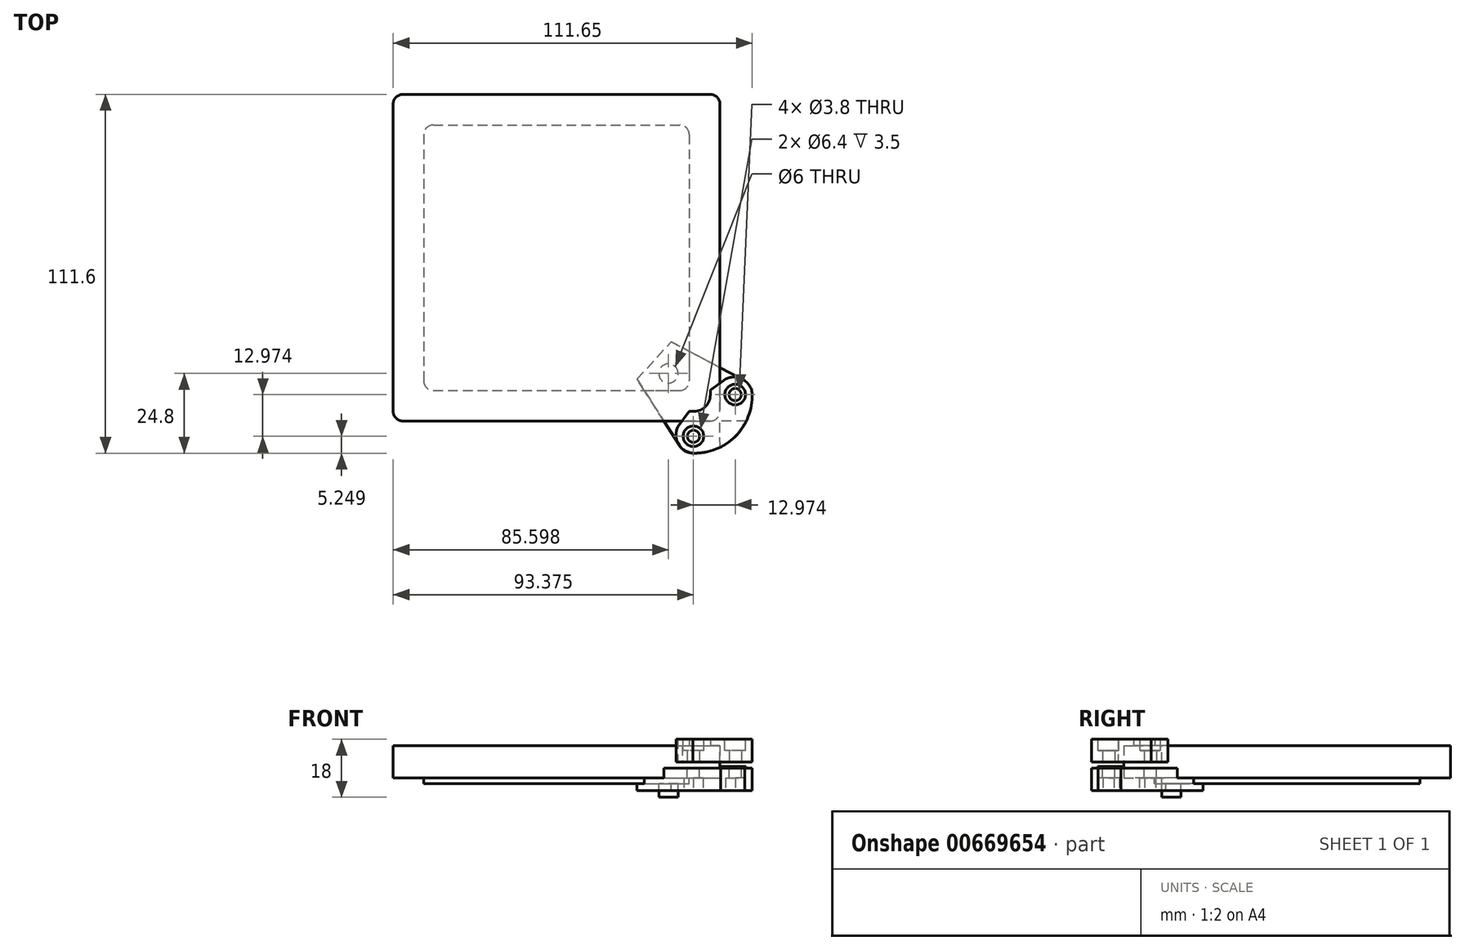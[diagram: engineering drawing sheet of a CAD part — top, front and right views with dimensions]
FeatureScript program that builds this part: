
annotation { "Feature Type Name" : "Feature", "Feature Type Description" : "" }
export const myFeature = defineFeature(function(context is Context, id is Id, definition is map)
    precondition{}
    {
        {
            var Q0;
            Q0=qCreatedBy(makeId("Top.planeOp"),FACE);
            var sketch = newSketch(context, id + "F0", { "sketchPlane" : qUnion([Q0])});
            skLineSegment(sketch, "E0.bottom", {"start": v(-49.2, 52.24) * mm, "end": v(46.4, 52.24) * mm});
            skLineSegment(sketch, "E0.top", {"start": v(-49.2, -49.36) * mm, "end": v(46.4, -49.36) * mm});
            skLineSegment(sketch, "E0.left", {"start": v(-52.2, 49.24) * mm, "end": v(-52.2, -46.36) * mm});
            skLineSegment(sketch, "E0.right", {"start": v(49.4, 49.24) * mm, "end": v(49.4, -46.36) * mm});
            skPoint(sketch, "E1.visualSharp", {"position": v(-52.2, 52.24) * mm});
            skArc(sketch, "E1.filletArc", {"start": v(-49.2, 52.24) * mm, "mid": v(-51.31, 51.36) * mm, "end": v(-52.2, 49.24) * mm});
            skPoint(sketch, "E2.visualSharp", {"position": v(-52.2, -49.36) * mm});
            skArc(sketch, "E2.filletArc", {"start": v(-52.2, -46.36) * mm, "mid": v(-51.31, -48.48) * mm, "end": v(-49.2, -49.36) * mm});
            skPoint(sketch, "E3.visualSharp", {"position": v(49.4, -49.36) * mm});
            skArc(sketch, "E3.filletArc", {"start": v(46.4, -49.36) * mm, "mid": v(48.53, -48.48) * mm, "end": v(49.4, -46.36) * mm});
            skPoint(sketch, "E4.visualSharp", {"position": v(49.4, 52.24) * mm});
            skArc(sketch, "E4.filletArc", {"start": v(49.4, 49.24) * mm, "mid": v(48.53, 51.36) * mm, "end": v(46.4, 52.24) * mm});
            skLineSegment(sketch, "E5.0", {"start": v(-39.7, 42.74) * mm, "end": v(36.9, 42.74) * mm});
            skLineSegment(sketch, "E5.1", {"start": v(-42.7, 39.74) * mm, "end": v(-42.7, -36.86) * mm});
            skLineSegment(sketch, "E5.2", {"start": v(-39.7, -39.86) * mm, "end": v(36.9, -39.86) * mm});
            skLineSegment(sketch, "E5.3", {"start": v(39.9, 39.74) * mm, "end": v(39.9, -36.86) * mm});
            skPoint(sketch, "E6.visualSharp", {"position": v(-42.7, 42.74) * mm});
            skArc(sketch, "E6.filletArc", {"start": v(-39.7, 42.74) * mm, "mid": v(-41.81, 41.86) * mm, "end": v(-42.7, 39.74) * mm});
            skPoint(sketch, "E7.visualSharp", {"position": v(-42.7, -39.86) * mm});
            skArc(sketch, "E7.filletArc", {"start": v(-42.7, -36.86) * mm, "mid": v(-41.81, -38.98) * mm, "end": v(-39.7, -39.86) * mm});
            skPoint(sketch, "E8.visualSharp", {"position": v(39.9, -39.86) * mm});
            skArc(sketch, "E8.filletArc", {"start": v(36.9, -39.86) * mm, "mid": v(39.03, -38.98) * mm, "end": v(39.9, -36.86) * mm});
            skPoint(sketch, "E9.visualSharp", {"position": v(39.9, 42.74) * mm});
            skArc(sketch, "E9.filletArc", {"start": v(39.9, 39.74) * mm, "mid": v(39.03, 41.86) * mm, "end": v(36.9, 42.74) * mm});
            skCircle(sketch, "E10", {"center": v(33.4, -34.56) * mm, "radius": 3 * mm});
            skSolve(sketch);
        }
        {
            var Q0;
            Q0 = qSketchRegion(id + "F0", true);
            var Q1;
            Q1=makeQuery(id+"F0.imprint","IMPRINT",FACE,{"disambiguationData":[TD([[makeQuery(id+"F0.imprint","IMPRINT",EDGE,{"derivedFrom":sQuery(id+"F0.wireOp",EDGE,"E5.0")}),-1.0]])]});
            var Q2;
            Q2=makeQuery(id+"F0.imprint","IMPRINT",FACE,{"disambiguationData":[TD([[makeQuery(id+"F0.imprint","IMPRINT",EDGE,{"derivedFrom":sQuery(id+"F0.wireOp",EDGE,"E10")}),1.0]])]});
            extrude(context, id + "F1", {"entities" : qUnion([Q0, Q1, Q2]), "flatOperationType" : FlatOperationType.REMOVE, "depth" : 10 * mm, "offsetDistance" : 25.4 * mm, "domain" : OperationDomain.MODEL});
        }
        {
            var Q0;
            Q0=makeQuery(id+"F0.imprint","IMPRINT",FACE,{"disambiguationData":[TD([[makeQuery(id+"F0.imprint","IMPRINT",EDGE,{"derivedFrom":sQuery(id+"F0.wireOp",EDGE,"E5.0")}),-1.0]])]});
            extrude(context, id + "F2", {"entities" : qUnion([Q0]), "operationType" : NewBodyOperationType.ADD, "oppositeDirection" : true, "depth" : 1.8 * mm, "offsetDistance" : 25 * mm});
        }
        {
            var Q0;
            Q0=makeQuery(id+"F2.boolean.opBoolean","SPLIT",FACE,{"disambiguationData":[TD([makeQuery(id+"F2.opExtrude","SWEPT_FACE",FACE,{"disambiguationData":[OSD([sQuery(id+"F0.wireOp",EDGE,"E10")])]})])],"derivedFrom":makeQuery(id+"F1.opExtrude","CAP_FACE",FACE,{"disambiguationData":[OSD([sQuery(id+"F0.wireOp",EDGE,"E0.bottom"),sQuery(id+"F0.wireOp",EDGE,"E0.top"),sQuery(id+"F0.wireOp",EDGE,"E0.left"),sQuery(id+"F0.wireOp",EDGE,"E0.right"),sQuery(id+"F0.wireOp",EDGE,"E1.filletArc"),sQuery(id+"F0.wireOp",EDGE,"E2.filletArc"),sQuery(id+"F0.wireOp",EDGE,"E3.filletArc"),sQuery(id+"F0.wireOp",EDGE,"E4.filletArc")])],"isStart":true})});
            var Q1;
            Q1=sQuery(id+"F0.wireOp",EDGE,"E10");
            extrude(context, id + "F3", {"entities" : qUnion([Q0]), "operationType" : NewBodyOperationType.ADD, "surfaceEntities" : qUnion([Q1]), "depth" : 6 * mm, "offsetDistance" : 25 * mm});
        }
        {
            var Q0;
            Q0=qCreatedBy(makeId("Top.planeOp"),FACE);
            var sketch = newSketch(context, id + "F4", { "sketchPlane" : qUnion([Q0])});
            skLineSegment(sketch, "E11.bottom", {"start": v(56.62, -36.5) * mm, "end": v(34.3, -24.68) * mm});
            skLineSegment(sketch, "E11.top", {"start": v(41.5, -59.36) * mm, "end": v(41.18, -59.36) * mm});
            skLineSegment(sketch, "E11.left", {"start": v(59.4, -41.14) * mm, "end": v(59.4, -41.45) * mm});
            skLineSegment(sketch, "E11.right", {"start": v(23.66, -36.34) * mm, "end": v(36.76, -56.93) * mm});
            skArc(sketch, "E12.filletArc", {"start": v(36.76, -56.93) * mm, "mid": v(38.66, -58.71) * mm, "end": v(41.18, -59.36) * mm});
            skArc(sketch, "E13.filletArc", {"start": v(41.5, -59.36) * mm, "mid": v(54.16, -54.11) * mm, "end": v(59.4, -41.45) * mm});
            skArc(sketch, "E14.filletArc", {"start": v(59.4, -41.14) * mm, "mid": v(58.66, -38.43) * mm, "end": v(56.62, -36.5) * mm});
            skCircle(sketch, "E15", {"center": v(54.16, -41.14) * mm, "radius": 1.9 * mm});
            skCircle(sketch, "E16", {"center": v(41.18, -54.11) * mm, "radius": 1.9 * mm});
            skPoint(sketch, "E17", {"position": v(34.3, -24.68) * mm});
            skPoint(sketch, "E18", {"position": v(23.66, -36.34) * mm});
            skLineSegment(sketch, "E19", {"start": v(34.3, -24.68) * mm, "end": v(23.66, -36.34) * mm});
            skPoint(sketch, "E20", {"position": v(41.18, -59.36) * mm});
            skLineSegment(sketch, "E21", {"start": v(30.2, -46.63) * mm, "end": v(45.46, -30.59) * mm, "construction": true});
            skLineSegment(sketch, "E22", {"start": v(37.83, -38.61) * mm, "end": v(28.98, -30.5) * mm, "construction": true});
            skPoint(sketch, "E23", {"position": v(33.4, -34.56) * mm});
            skLineSegment(sketch, "E24", {"start": v(36.76, -56.93) * mm, "end": v(56.62, -36.5) * mm, "construction": true});
            skLineSegment(sketch, "E25", {"start": v(32.03, -49.5) * mm, "end": v(70.12, -49.5) * mm, "construction": true});
            skLineSegment(sketch, "E26", {"start": v(49.4, -63.01) * mm, "end": v(49.4, -15.8) * mm, "construction": true});
            skLineSegment(sketch, "E27", {"start": v(49.4, -49.5) * mm, "end": v(49.4, -57.52) * mm});
            skLineSegment(sketch, "E28", {"start": v(49.4, -49.5) * mm, "end": v(57.5, -49.5) * mm});
            skEllipticalArc(sketch, "E29", {});
            skLineSegment(sketch, "E30", {"start": v(49.4, -57.5) * mm, "end": v(49.4, -49.5) * mm});
            const initialGuessF4  = {"E29": [0.049408, -0.0494937938059676, 0.7031298044576713, -0.7110615149783577, 0.006693227332354382, 0.010739871215108025, 5.730894756647801, 0.562360824754581]};
            skSetInitialGuess(sketch, initialGuessF4);
            skSolve(sketch);
        }
        {
            var Q0;
            Q0 = qSketchRegion(id + "F4", true);
            extrude(context, id + "F5", {"entities" : qUnion([Q0]), "oppositeDirection" : true, "depth" : 7 * mm, "offsetDistance" : 25 * mm});
        }
        {
            var Q0;
            Q0=makeQuery(id+"F5.opExtrude","SWEPT_BODY",BODY,{"disambiguationData":[OSD([sQuery(id+"F4.wireOp",EDGE,"E11.bottom"),sQuery(id+"F4.wireOp",EDGE,"E11.top"),sQuery(id+"F4.wireOp",EDGE,"E11.left"),sQuery(id+"F4.wireOp",EDGE,"E11.right"),sQuery(id+"F4.wireOp",EDGE,"E12.filletArc"),sQuery(id+"F4.wireOp",EDGE,"E13.filletArc"),sQuery(id+"F4.wireOp",EDGE,"E14.filletArc"),sQuery(id+"F4.wireOp",EDGE,"E15"),sQuery(id+"F4.wireOp",EDGE,"E16"),sQuery(id+"F4.wireOp",EDGE,"66c13378-0b8c-4c4a-871f-ac784376b0e9"),sQuery(id+"F4.wireOp",EDGE,"E19")])]});
            transform(context, id + "F6", {"entities" : qUnion([Q0]), "transformType" : TransformType.TRANSLATION_3D, "dx" : 0 * mm, "dy" : 0 * mm, "dz" : 3 * mm, "makeCopy" : false});
        }
        {
            var Q0;
            Q0=makeQuery(id+"F5.opExtrude","CAP_FACE",FACE,{"disambiguationData":[OSD([sQuery(id+"F4.wireOp",EDGE,"E11.bottom"),sQuery(id+"F4.wireOp",EDGE,"E11.top"),sQuery(id+"F4.wireOp",EDGE,"E11.left"),sQuery(id+"F4.wireOp",EDGE,"E11.right"),sQuery(id+"F4.wireOp",EDGE,"E12.filletArc"),sQuery(id+"F4.wireOp",EDGE,"E13.filletArc"),sQuery(id+"F4.wireOp",EDGE,"E14.filletArc"),sQuery(id+"F4.wireOp",EDGE,"E15"),sQuery(id+"F4.wireOp",EDGE,"E16"),sQuery(id+"F4.wireOp",EDGE,"E19")])],"isStart":false});
            var sketch = newSketch(context, id + "F7", { "sketchPlane" : qUnion([Q0])});
            skCircle(sketch, "E31.cCircle", {"center": v(54.16, 41.14) * mm, "radius": 3.4 * mm, "construction": true});
            skLineSegment(sketch, "E31.0", {"start": v(51.2, 42.84) * mm, "end": v(54.16, 44.54) * mm});
            skLineSegment(sketch, "E31.1", {"start": v(54.16, 44.54) * mm, "end": v(57.1, 42.84) * mm});
            skLineSegment(sketch, "E31.2", {"start": v(57.1, 42.84) * mm, "end": v(57.1, 39.43) * mm});
            skLineSegment(sketch, "E31.3", {"start": v(57.1, 39.43) * mm, "end": v(54.16, 37.73) * mm});
            skLineSegment(sketch, "E31.4", {"start": v(54.16, 37.73) * mm, "end": v(51.2, 39.43) * mm});
            skLineSegment(sketch, "E31.5", {"start": v(51.2, 39.43) * mm, "end": v(51.2, 42.84) * mm});
            skCircle(sketch, "E32.cCircle", {"center": v(41.18, 54.11) * mm, "radius": 3.4 * mm, "construction": true});
            skLineSegment(sketch, "E32.0", {"start": v(38.23, 55.81) * mm, "end": v(41.18, 57.52) * mm});
            skLineSegment(sketch, "E32.1", {"start": v(41.18, 57.52) * mm, "end": v(44.13, 55.81) * mm});
            skLineSegment(sketch, "E32.2", {"start": v(44.13, 55.81) * mm, "end": v(44.13, 52.4) * mm});
            skLineSegment(sketch, "E32.3", {"start": v(44.13, 52.4) * mm, "end": v(41.18, 50.7) * mm});
            skLineSegment(sketch, "E32.4", {"start": v(41.18, 50.7) * mm, "end": v(38.23, 52.4) * mm});
            skLineSegment(sketch, "E32.5", {"start": v(38.23, 52.4) * mm, "end": v(38.23, 55.81) * mm});
            skSolve(sketch);
        }
        {
            var Q0;
            Q0 = qSketchRegion(id + "F7", true);
            extrude(context, id + "F8", {"entities" : qUnion([Q0]), "operationType" : NewBodyOperationType.REMOVE, "oppositeDirection" : true, "depth" : 4 * mm, "offsetDistance" : 25 * mm});
        }
        {
            var Q0;
            Q0=makeQuery(id+"F1.opExtrude","CAP_FACE",FACE,{"disambiguationData":[OSD([sQuery(id+"F0.wireOp",EDGE,"E0.bottom"),sQuery(id+"F0.wireOp",EDGE,"E0.top"),sQuery(id+"F0.wireOp",EDGE,"E0.left"),sQuery(id+"F0.wireOp",EDGE,"E0.right"),sQuery(id+"F0.wireOp",EDGE,"E1.filletArc"),sQuery(id+"F0.wireOp",EDGE,"E2.filletArc"),sQuery(id+"F0.wireOp",EDGE,"E3.filletArc"),sQuery(id+"F0.wireOp",EDGE,"E4.filletArc")])],"isStart":false});
            var sketch = newSketch(context, id + "F9", { "sketchPlane" : qUnion([Q0])});
            skArc(sketch, "E33.filletArc", {"start": v(41.06, -59.34) * mm, "mid": v(54.24, -54.07) * mm, "end": v(59.45, -40.86) * mm});
            skPoint(sketch, "E34", {"position": v(34.12, -59.33) * mm});
            skCircle(sketch, "E35", {"center": v(54.16, -41.14) * mm, "radius": 1.9 * mm});
            skCircle(sketch, "E36", {"center": v(41.18, -54.11) * mm, "radius": 1.9 * mm});
            skLineSegment(sketch, "E37", {"start": v(50.52, -36.75) * mm, "end": v(46.4, -39.68) * mm});
            skLineSegment(sketch, "E38", {"start": v(46.4, -39.68) * mm, "end": v(46.4, -41.3) * mm});
            skPoint(sketch, "E39.visualSharp", {"position": v(56.89, -32.2) * mm});
            skArc(sketch, "E39.filletArc", {"start": v(59.45, -40.86) * mm, "mid": v(56.17, -36.21) * mm, "end": v(50.52, -36.75) * mm});
            skLineSegment(sketch, "E40", {"start": v(54.24, -54.07) * mm, "end": v(41.55, -41.44) * mm, "construction": true});
            skLineSegment(sketch, "E41.MirrorCS", {"start": v(39.82, -46.31) * mm, "end": v(41.43, -46.3) * mm});
            skLineSegment(sketch, "E42.MirrorCS", {"start": v(36.37, -51.19) * mm, "end": v(39.82, -46.31) * mm});
            skArc(sketch, "E43.MirrorCS", {"start": v(41.06, -59.34) * mm, "mid": v(36.53, -56.52) * mm, "end": v(36.37, -51.19) * mm});
            skPoint(sketch, "E44.visualSharp", {"position": v(46.4, -46.28) * mm});
            skArc(sketch, "E44.filletArc", {"start": v(41.43, -46.3) * mm, "mid": v(44.95, -44.83) * mm, "end": v(46.4, -41.3) * mm});
            skSolve(sketch);
        }
        {
            var Q0;
            Q0 = qSketchRegion(id + "F9", true);
            extrude(context, id + "F10", {"entities" : qUnion([Q0]), "depth" : 7 * mm, "offsetDistance" : 25 * mm});
        }
        {
            var Q0;
            Q0=makeQuery(id+"F10.opExtrude","CAP_FACE",FACE,{"disambiguationData":[OSD([sQuery(id+"F9.wireOp",EDGE,"a39b41d0-e7ae-40f5-bbe2-d8dd226e776d.bottom"),sQuery(id+"F9.wireOp",EDGE,"a39b41d0-e7ae-40f5-bbe2-d8dd226e776d.top"),sQuery(id+"F9.wireOp",EDGE,"a39b41d0-e7ae-40f5-bbe2-d8dd226e776d.left"),sQuery(id+"F9.wireOp",EDGE,"a39b41d0-e7ae-40f5-bbe2-d8dd226e776d.right"),sQuery(id+"F9.wireOp",EDGE,"845669e1-6970-4c6b-b3a8-32a38f3c468b.filletArc"),sQuery(id+"F9.wireOp",EDGE,"E33.filletArc"),sQuery(id+"F9.wireOp",EDGE,"ea5769c7-4f24-4bfb-a007-04b614ccd4af.filletArc"),sQuery(id+"F9.wireOp",EDGE,"E35"),sQuery(id+"F9.wireOp",EDGE,"E36")])],"isStart":false});
            var sketch = newSketch(context, id + "F11", { "sketchPlane" : qUnion([Q0])});
            skCircle(sketch, "E45", {"center": v(41.18, -54.11) * mm, "radius": 3.2 * mm});
            skCircle(sketch, "E46", {"center": v(54.16, -41.14) * mm, "radius": 3.2 * mm});
            skSolve(sketch);
        }
        {
            var Q0;
            Q0 = qSketchRegion(id + "F11", true);
            extrude(context, id + "F12", {"entities" : qUnion([Q0]), "operationType" : NewBodyOperationType.REMOVE, "oppositeDirection" : true, "depth" : 3.5 * mm, "offsetDistance" : 25 * mm});
        }
        {
            var Q0;
            Q0=makeQuery(id+"F10.opExtrude","SWEPT_BODY",BODY,{"disambiguationData":[OSD([sQuery(id+"F9.wireOp",EDGE,"a39b41d0-e7ae-40f5-bbe2-d8dd226e776d.bottom"),sQuery(id+"F9.wireOp",EDGE,"a39b41d0-e7ae-40f5-bbe2-d8dd226e776d.top"),sQuery(id+"F9.wireOp",EDGE,"a39b41d0-e7ae-40f5-bbe2-d8dd226e776d.left"),sQuery(id+"F9.wireOp",EDGE,"a39b41d0-e7ae-40f5-bbe2-d8dd226e776d.right"),sQuery(id+"F9.wireOp",EDGE,"845669e1-6970-4c6b-b3a8-32a38f3c468b.filletArc"),sQuery(id+"F9.wireOp",EDGE,"E33.filletArc"),sQuery(id+"F9.wireOp",EDGE,"ea5769c7-4f24-4bfb-a007-04b614ccd4af.filletArc"),sQuery(id+"F9.wireOp",EDGE,"E35"),sQuery(id+"F9.wireOp",EDGE,"E36")])]});
            transform(context, id + "F13", {"entities" : qUnion([Q0]), "transformType" : TransformType.TRANSLATION_3D, "dx" : 0 * mm, "dy" : 0 * mm, "dz" : -5 * mm, "makeCopy" : false});
        }
        {
            var Q0;
            Q0=makeQuery(id+"F1.opExtrude","SWEPT_BODY",BODY,{"disambiguationData":[OSD([sQuery(id+"F0.wireOp",EDGE,"E0.bottom"),sQuery(id+"F0.wireOp",EDGE,"E0.top"),sQuery(id+"F0.wireOp",EDGE,"E0.left"),sQuery(id+"F0.wireOp",EDGE,"E0.right"),sQuery(id+"F0.wireOp",EDGE,"E1.filletArc"),sQuery(id+"F0.wireOp",EDGE,"E2.filletArc"),sQuery(id+"F0.wireOp",EDGE,"E3.filletArc"),sQuery(id+"F0.wireOp",EDGE,"E4.filletArc")])]});
            var Q1;
            Q1=makeQuery(id+"F10.opExtrude","SWEPT_BODY",BODY,{"disambiguationData":[OSD([sQuery(id+"F9.wireOp",EDGE,"a39b41d0-e7ae-40f5-bbe2-d8dd226e776d.bottom"),sQuery(id+"F9.wireOp",EDGE,"a39b41d0-e7ae-40f5-bbe2-d8dd226e776d.top"),sQuery(id+"F9.wireOp",EDGE,"a39b41d0-e7ae-40f5-bbe2-d8dd226e776d.left"),sQuery(id+"F9.wireOp",EDGE,"a39b41d0-e7ae-40f5-bbe2-d8dd226e776d.right"),sQuery(id+"F9.wireOp",EDGE,"845669e1-6970-4c6b-b3a8-32a38f3c468b.filletArc"),sQuery(id+"F9.wireOp",EDGE,"E33.filletArc"),sQuery(id+"F9.wireOp",EDGE,"ea5769c7-4f24-4bfb-a007-04b614ccd4af.filletArc"),sQuery(id+"F9.wireOp",EDGE,"E35"),sQuery(id+"F9.wireOp",EDGE,"E36")])]});
            booleanBodies(context, id + "F14", {"operationType" : BooleanOperationType.SUBTRACTION, "tools" : qUnion([Q0]), "targets" : qUnion([Q1]), "keepTools" : true});
        }
        {
            var Q0;
            Q0=makeQuery(id+"F1.opExtrude","SWEPT_BODY",BODY,{"disambiguationData":[OSD([sQuery(id+"F0.wireOp",EDGE,"E0.bottom"),sQuery(id+"F0.wireOp",EDGE,"E0.top"),sQuery(id+"F0.wireOp",EDGE,"E0.left"),sQuery(id+"F0.wireOp",EDGE,"E0.right"),sQuery(id+"F0.wireOp",EDGE,"E1.filletArc"),sQuery(id+"F0.wireOp",EDGE,"E2.filletArc"),sQuery(id+"F0.wireOp",EDGE,"E3.filletArc"),sQuery(id+"F0.wireOp",EDGE,"E4.filletArc")])]});
            var Q1;
            Q1=makeQuery(id+"F5.opExtrude","SWEPT_BODY",BODY,{"disambiguationData":[OSD([sQuery(id+"F4.wireOp",EDGE,"E11.bottom"),sQuery(id+"F4.wireOp",EDGE,"E11.top"),sQuery(id+"F4.wireOp",EDGE,"E11.left"),sQuery(id+"F4.wireOp",EDGE,"E11.right"),sQuery(id+"F4.wireOp",EDGE,"E12.filletArc"),sQuery(id+"F4.wireOp",EDGE,"E13.filletArc"),sQuery(id+"F4.wireOp",EDGE,"E14.filletArc"),sQuery(id+"F4.wireOp",EDGE,"E15"),sQuery(id+"F4.wireOp",EDGE,"E16"),sQuery(id+"F4.wireOp",EDGE,"E19")])]});
            booleanBodies(context, id + "F15", {"operationType" : BooleanOperationType.SUBTRACTION, "tools" : qUnion([Q0]), "targets" : qUnion([Q1]), "keepTools" : true});
        }
        {
            var Q0;
            Q0=makeQuery(id+"F5.opExtrude","CAP_FACE",FACE,{"disambiguationData":[OSD([sQuery(id+"F4.wireOp",EDGE,"E11.bottom"),sQuery(id+"F4.wireOp",EDGE,"E11.top"),sQuery(id+"F4.wireOp",EDGE,"E11.left"),sQuery(id+"F4.wireOp",EDGE,"E11.right"),sQuery(id+"F4.wireOp",EDGE,"E12.filletArc"),sQuery(id+"F4.wireOp",EDGE,"E13.filletArc"),sQuery(id+"F4.wireOp",EDGE,"E14.filletArc"),sQuery(id+"F4.wireOp",EDGE,"E15"),sQuery(id+"F4.wireOp",EDGE,"E16"),sQuery(id+"F4.wireOp",EDGE,"E19"),sQuery(id+"F4.wireOp",EDGE,"E29")])],"isStart":true});
            var sketch = newSketch(context, id + "F16", { "sketchPlane" : qUnion([Q0])});
            skLineSegment(sketch, "E47", {"start": v(32.14, -49.41) * mm, "end": v(70.24, -49.41) * mm, "construction": true});
            skLineSegment(sketch, "E48", {"start": v(49.4, -67.66) * mm, "end": v(49.4, -31.15) * mm, "construction": true});
            skEllipticalArc(sketch, "E49", {});
            skLineSegment(sketch, "E50", {"start": v(49.46, -57.49) * mm, "end": v(49.4, -49.36) * mm});
            skLineSegment(sketch, "E51", {"start": v(57.57, -49.41) * mm, "end": v(49.4, -49.36) * mm});
            const initialGuessF16  = {"E49": [0.049408, -0.04936, 0.7031298044576713, -0.7110615149783577, 0.006804975713047634, 0.010919181308363177, 5.7363346115275835, 0.5568305108967264]};
            skSetInitialGuess(sketch, initialGuessF16);
            skSolve(sketch);
        }
        {
            var Q0;
            Q0 = qSketchRegion(id + "F16", true);
            extrude(context, id + "F17", {"entities" : qUnion([Q0]), "operationType" : NewBodyOperationType.ADD, "depth" : .5 * mm, "offsetDistance" : 25 * mm});
        }
    });
